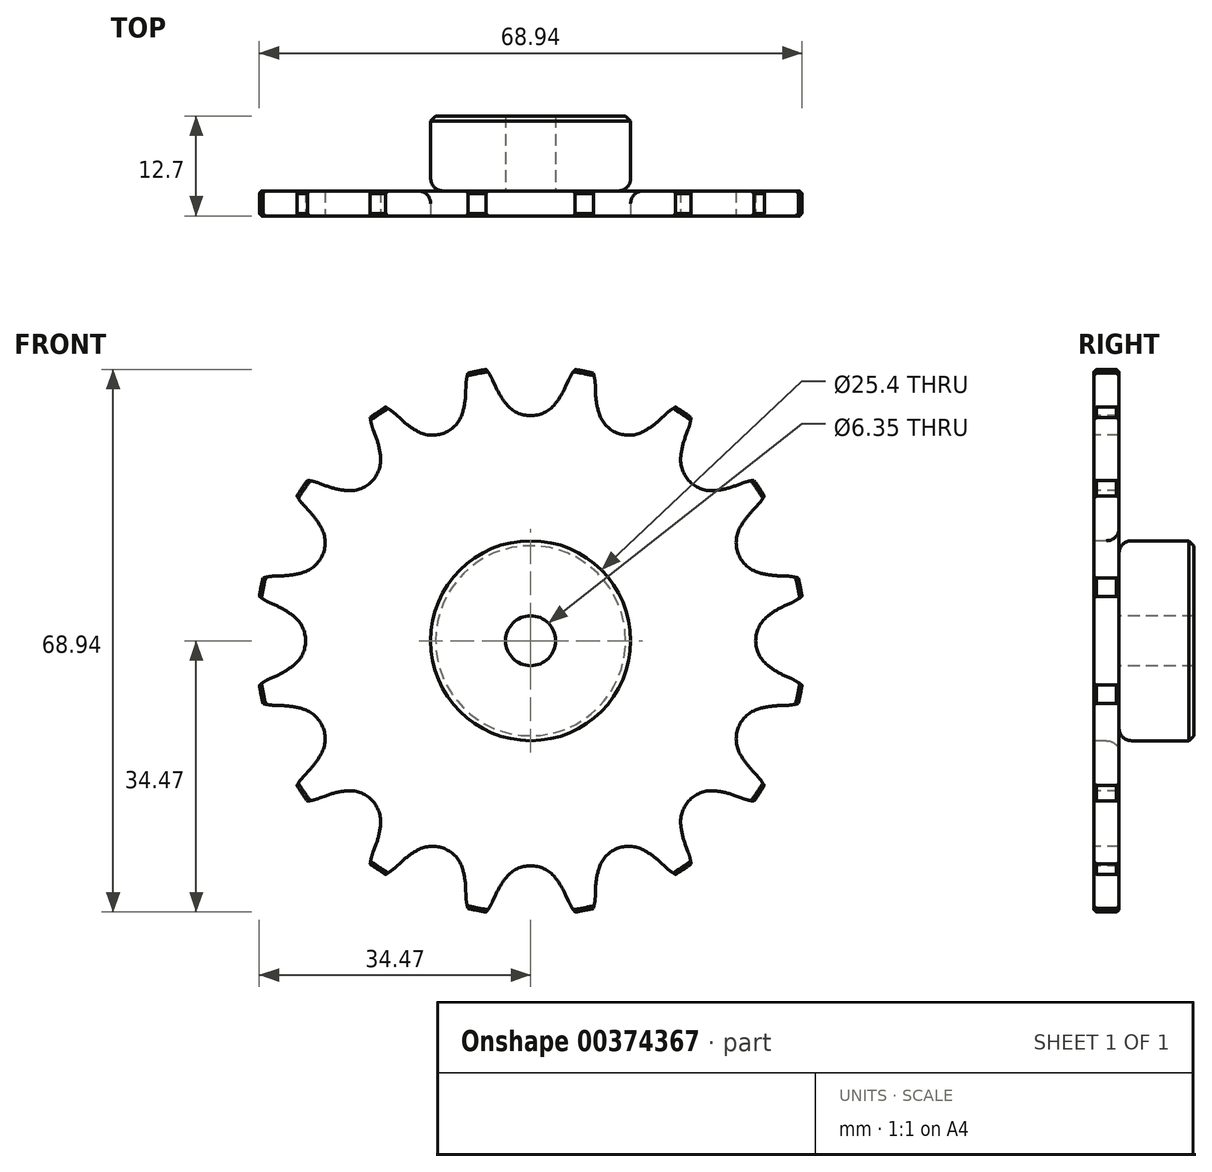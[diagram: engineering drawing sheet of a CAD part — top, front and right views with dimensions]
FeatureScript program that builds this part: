
annotation { "Feature Type Name" : "Feature", "Feature Type Description" : "" }
export const myFeature = defineFeature(function(context is Context, id is Id, definition is map)
    precondition{}
    {
        {
            assignVariable(context, id + "F0", {"name" : "Chamfer1Radius", "anyValue" : 0.64 * mm});
        }
        {
            var Q0;
            Q0=qCreatedBy(makeId("Right.planeOp"),FACE);
            var sketch = newSketch(context, id + "F1", { "sketchPlane" : qUnion([Q0])});
            skLineSegment(sketch, "E0", {"start": v(0, 0) * mm, "end": v(12.7, 0) * mm});
            skLineSegment(sketch, "E1.bottom", {"start": v(0, 3.18) * mm, "end": v(3.17, 3.18) * mm});
            skLineSegment(sketch, "E1.top", {"start": v(0, 34.93) * mm, "end": v(3.18, 34.93) * mm});
            skLineSegment(sketch, "E1.left", {"start": v(0, 3.18) * mm, "end": v(0, 34.93) * mm});
            skLineSegment(sketch, "E1.right", {"start": v(3.18, 3.18) * mm, "end": v(3.17, 34.93) * mm});
            skLineSegment(sketch, "E2.bottom", {"start": v(0, 3.18) * mm, "end": v(12.7, 3.18) * mm});
            skLineSegment(sketch, "E2.top", {"start": v(0, 12.7) * mm, "end": v(12.7, 12.7) * mm});
            skLineSegment(sketch, "E2.left", {"start": v(0, 3.18) * mm, "end": v(0, 12.7) * mm});
            skLineSegment(sketch, "E2.right", {"start": v(12.7, 3.18) * mm, "end": v(12.7, 12.7) * mm});
            skLineSegment(sketch, "E3.MirrorCS", {"start": v(0, -3.18) * mm, "end": v(3.17, -3.18) * mm});
            skLineSegment(sketch, "E4.MirrorCS", {"start": v(0, -12.7) * mm, "end": v(12.7, -12.7) * mm});
            skLineSegment(sketch, "E5.MirrorCS", {"start": v(0, -3.18) * mm, "end": v(12.7, -3.18) * mm});
            skLineSegment(sketch, "E6.MirrorCS", {"start": v(12.7, -3.18) * mm, "end": v(12.7, -12.7) * mm});
            skLineSegment(sketch, "E7.MirrorCS", {"start": v(3.18, -3.18) * mm, "end": v(3.18, -34.93) * mm});
            skLineSegment(sketch, "E8.MirrorCS", {"start": v(0, -3.18) * mm, "end": v(0, -34.93) * mm});
            skLineSegment(sketch, "E9.MirrorCS", {"start": v(0, -34.93) * mm, "end": v(3.18, -34.93) * mm});
            skLineSegment(sketch, "E10.MirrorCS", {"start": v(0, -3.18) * mm, "end": v(0, -12.7) * mm});
            skSolve(sketch);
        }
        {
            var Q0;
            {var subQ5=sQuery(id+"F1.wireOp",EDGE,"E2.right");Q0=makeQuery(id+"F1.imprint","IMPRINT",FACE,{"disambiguationData":[TD([[makeQuery(id+"F1.imprint","IMPRINT",EDGE,{"derivedFrom":subQ5}),1.0]])]});}
            var Q1;
            {var subQ5=sQuery(id+"F1.wireOp",EDGE,"E2.left");Q1=makeQuery(id+"F1.imprint","IMPRINT",FACE,{"disambiguationData":[TD([[makeQuery(id+"F1.imprint","IMPRINT",EDGE,{"derivedFrom":subQ5}),-1.0]])]});}
            var Q2;
            {var subQ0=sQuery(id+"F1.wireOp",EDGE,"E1.top");Q2=makeQuery(id+"F1.imprint","IMPRINT",FACE,{"disambiguationData":[TD([[makeQuery(id+"F1.imprint","IMPRINT",EDGE,{"derivedFrom":subQ0}),-1.0]])]});}
            var Q3;
            Q3=sQuery(id+"F1.wireOp",EDGE,"E0");
            revolve(context, id + "F2", {"entities" : qUnion([Q0, Q1, Q2]), "axis" : qUnion([Q3]), "revolveType" : RevolveType.FULL});
        }
        {
            var Q0;
            Q0=makeQuery(id+"F2.opRevolve","SWEPT_EDGE",EDGE,{"disambiguationData":[OSD([sQuery(id+"F1.wireOp",EDGE,"E1.right"),sQuery(id+"F1.wireOp",EDGE,"E2.top")])]});
            fillet(context, id + "F3", {"entities" : qUnion([Q0]), "radius" : 1.59 * mm, "tangentPropagation" : true, "allowEdgeOverflow" : false});
        }
        {
            var Q0;
            Q0=makeQuery(id+"F2.opRevolve","SWEPT_EDGE",EDGE,{"disambiguationData":[OSD([sQuery(id+"F1.wireOp",EDGE,"E2.top"),sQuery(id+"F1.wireOp",EDGE,"E2.right")])]});
            chamfer(context, id + "F4", {"entities" : qUnion([Q0]), "width" : getVariable(context, 'Chamfer1Radius'), "tangentPropagation" : true});
        }
        {
            var Q0;
            Q0=makeQuery(id+"F2.opRevolve","SWEPT_EDGE",EDGE,{"disambiguationData":[OSD([sQuery(id+"F1.wireOp",EDGE,"E1.top"),sQuery(id+"F1.wireOp",EDGE,"E1.left")])]});
            var Q1;
            Q1=makeQuery(id+"F2.opRevolve","SWEPT_EDGE",EDGE,{"disambiguationData":[OSD([sQuery(id+"F1.wireOp",EDGE,"E1.top"),sQuery(id+"F1.wireOp",EDGE,"E1.right")])]});
            chamfer(context, id + "F5", {"entities" : qUnion([Q0, Q1]), "width" : 0.32 * mm, "tangentPropagation" : true});
        }
        {
            var Q0;
            Q0=makeQuery(id+"F2.opRevolve","SWEPT_FACE",FACE,{"disambiguationData":[OSD([sQuery(id+"F1.wireOp",EDGE,"E1.left"),sQuery(id+"F1.wireOp",EDGE,"E2.left")])]});
            var sketch = newSketch(context, id + "F6", { "sketchPlane" : qUnion([Q0])});
            skCircle(sketch, "E11", {"center": v(0, 0) * mm, "radius": 32.55 * mm, "construction": true});
            skLineSegment(sketch, "E12", {"start": v(0, 0) * mm, "end": v(0, 32.55) * mm, "construction": true});
            skLineSegment(sketch, "E13", {"start": v(47.22, 32.55) * mm, "end": v(0, 32.55) * mm, "construction": true});
            skLineSegment(sketch, "E14", {"start": v(0, 32.55) * mm, "end": v(5, 36.56) * mm, "construction": true});
            skLineSegment(sketch, "E15", {"start": v(5, 36.56) * mm, "end": v(-4.46, 32.3) * mm, "construction": true});
            skLineSegment(sketch, "E16", {"start": v(-4.46, 32.3) * mm, "end": v(-4.82, 33.1) * mm});
            skLineSegment(sketch, "E17", {"start": v(0, 0) * mm, "end": v(-7.13, 35.85) * mm, "construction": true});
            skArc(sketch, "E18", {"start": v(-7.13, 35.85) * mm, "mid": v(-15.87, 26.15) * mm, "end": v(-4.82, 33.1) * mm, "construction": true});
            skArc(sketch, "E19", {"start": v(-4.82, 33.1) * mm, "mid": v(-5.78, 34.63) * mm, "end": v(-7.13, 35.85) * mm});
            skLineSegment(sketch, "E20", {"start": v(-4.82, 33.1) * mm, "end": v(-4.82, 33.1) * mm});
            skLineSegment(sketch, "E21", {"start": v(-4.46, 32.3) * mm, "end": v(-4.46, 32.3) * mm});
            skArc(sketch, "E22", {"start": v(-3.1, 30.07) * mm, "mid": v(13.83, 41.97) * mm, "end": v(-4.46, 32.3) * mm, "construction": true});
            skArc(sketch, "E23.MirrorCS", {"start": v(4.82, 33.1) * mm, "mid": v(5.78, 34.63) * mm, "end": v(7.13, 35.85) * mm});
            skArc(sketch, "E24.MirrorCS", {"start": v(4.46, 32.3) * mm, "mid": v(3.84, 31.14) * mm, "end": v(3.1, 30.07) * mm});
            skArc(sketch, "E25", {"start": v(-4.46, 32.3) * mm, "mid": v(-3.84, 31.14) * mm, "end": v(-3.1, 30.07) * mm});
            skLineSegment(sketch, "E26", {"start": v(-4.82, 33.1) * mm, "end": v(-11.63, 48.22) * mm, "construction": true});
            skLineSegment(sketch, "E27.MirrorCS", {"start": v(4.46, 32.3) * mm, "end": v(4.82, 33.1) * mm});
            skArc(sketch, "E28", {"start": v(3.1, 30.07) * mm, "mid": v(0, 36.51) * mm, "end": v(-3.1, 30.07) * mm, "construction": true});
            skArc(sketch, "E29", {"start": v(-3.1, 30.07) * mm, "mid": v(0, 28.59) * mm, "end": v(3.1, 30.07) * mm});
            skLineSegment(sketch, "E30.1.0", {"start": v(-16.48, 28.14) * mm, "end": v(-17.12, 28.74) * mm});
            skArc(sketch, "E30.1.1", {"start": v(-17.12, 28.74) * mm, "mid": v(-18.6, 29.79) * mm, "end": v(-20.3, 30.4) * mm});
            skArc(sketch, "E30.1.2", {"start": v(-14.36, 26.6) * mm, "mid": v(-10.94, 26.41) * mm, "end": v(-8.65, 28.96) * mm});
            skArc(sketch, "E30.1.3", {"start": v(-16.48, 28.14) * mm, "mid": v(-15.47, 27.3) * mm, "end": v(-14.36, 26.6) * mm});
            skArc(sketch, "E30.1.4", {"start": v(-8.24, 31.55) * mm, "mid": v(-8.37, 30.24) * mm, "end": v(-8.65, 28.96) * mm});
            skLineSegment(sketch, "E30.1.5", {"start": v(-8.24, 31.55) * mm, "end": v(-8.22, 32.42) * mm});
            skArc(sketch, "E30.1.6", {"start": v(-8.22, 32.42) * mm, "mid": v(-7.91, 34.21) * mm, "end": v(-7.13, 35.85) * mm});
            skLineSegment(sketch, "E30.2.0", {"start": v(-26, 19.69) * mm, "end": v(-26.8, 20) * mm});
            skArc(sketch, "E30.2.1", {"start": v(-26.8, 20) * mm, "mid": v(-28.58, 20.4) * mm, "end": v(-30.4, 20.3) * mm});
            skArc(sketch, "E30.2.2", {"start": v(-23.45, 19.08) * mm, "mid": v(-20.21, 20.21) * mm, "end": v(-19.08, 23.45) * mm});
            skArc(sketch, "E30.2.3", {"start": v(-26, 19.69) * mm, "mid": v(-24.74, 19.3) * mm, "end": v(-23.45, 19.08) * mm});
            skArc(sketch, "E30.2.4", {"start": v(-19.69, 26) * mm, "mid": v(-19.3, 24.74) * mm, "end": v(-19.08, 23.45) * mm});
            skLineSegment(sketch, "E30.2.5", {"start": v(-19.69, 26) * mm, "end": v(-20, 26.8) * mm});
            skArc(sketch, "E30.2.6", {"start": v(-20, 26.8) * mm, "mid": v(-20.4, 28.58) * mm, "end": v(-20.3, 30.4) * mm});
            skLineSegment(sketch, "E30.3.0", {"start": v(-31.55, 8.24) * mm, "end": v(-32.42, 8.22) * mm});
            skArc(sketch, "E30.3.1", {"start": v(-32.42, 8.22) * mm, "mid": v(-34.21, 7.91) * mm, "end": v(-35.85, 7.13) * mm});
            skArc(sketch, "E30.3.2", {"start": v(-28.96, 8.65) * mm, "mid": v(-26.41, 10.94) * mm, "end": v(-26.6, 14.36) * mm});
            skArc(sketch, "E30.3.3", {"start": v(-31.55, 8.24) * mm, "mid": v(-30.24, 8.37) * mm, "end": v(-28.96, 8.65) * mm});
            skArc(sketch, "E30.3.4", {"start": v(-28.14, 16.48) * mm, "mid": v(-27.3, 15.47) * mm, "end": v(-26.6, 14.36) * mm});
            skLineSegment(sketch, "E30.3.5", {"start": v(-28.14, 16.48) * mm, "end": v(-28.74, 17.12) * mm});
            skArc(sketch, "E30.3.6", {"start": v(-28.74, 17.12) * mm, "mid": v(-29.79, 18.6) * mm, "end": v(-30.4, 20.3) * mm});
            skLineSegment(sketch, "E30.4.0", {"start": v(-32.3, -4.46) * mm, "end": v(-33.1, -4.82) * mm});
            skArc(sketch, "E30.4.1", {"start": v(-33.1, -4.82) * mm, "mid": v(-34.63, -5.78) * mm, "end": v(-35.85, -7.13) * mm});
            skArc(sketch, "E30.4.2", {"start": v(-30.07, -3.1) * mm, "mid": v(-28.59, 0) * mm, "end": v(-30.07, 3.1) * mm});
            skArc(sketch, "E30.4.3", {"start": v(-32.3, -4.46) * mm, "mid": v(-31.14, -3.84) * mm, "end": v(-30.07, -3.1) * mm});
            skArc(sketch, "E30.4.4", {"start": v(-32.3, 4.46) * mm, "mid": v(-31.14, 3.84) * mm, "end": v(-30.07, 3.1) * mm});
            skLineSegment(sketch, "E30.4.5", {"start": v(-32.3, 4.46) * mm, "end": v(-33.1, 4.82) * mm});
            skArc(sketch, "E30.4.6", {"start": v(-33.1, 4.82) * mm, "mid": v(-34.63, 5.78) * mm, "end": v(-35.85, 7.13) * mm});
            skLineSegment(sketch, "E30.5.0", {"start": v(-28.14, -16.48) * mm, "end": v(-28.74, -17.12) * mm});
            skArc(sketch, "E30.5.1", {"start": v(-28.74, -17.12) * mm, "mid": v(-29.79, -18.6) * mm, "end": v(-30.4, -20.3) * mm});
            skArc(sketch, "E30.5.2", {"start": v(-26.6, -14.36) * mm, "mid": v(-26.41, -10.94) * mm, "end": v(-28.96, -8.65) * mm});
            skArc(sketch, "E30.5.3", {"start": v(-28.14, -16.48) * mm, "mid": v(-27.3, -15.47) * mm, "end": v(-26.6, -14.36) * mm});
            skArc(sketch, "E30.5.4", {"start": v(-31.55, -8.24) * mm, "mid": v(-30.24, -8.37) * mm, "end": v(-28.96, -8.65) * mm});
            skLineSegment(sketch, "E30.5.5", {"start": v(-31.55, -8.24) * mm, "end": v(-32.42, -8.22) * mm});
            skArc(sketch, "E30.5.6", {"start": v(-32.42, -8.22) * mm, "mid": v(-34.21, -7.91) * mm, "end": v(-35.85, -7.13) * mm});
            skLineSegment(sketch, "E30.6.0", {"start": v(-19.69, -26) * mm, "end": v(-20, -26.8) * mm});
            skArc(sketch, "E30.6.1", {"start": v(-20, -26.8) * mm, "mid": v(-20.4, -28.58) * mm, "end": v(-20.3, -30.4) * mm});
            skArc(sketch, "E30.6.2", {"start": v(-19.08, -23.45) * mm, "mid": v(-20.21, -20.21) * mm, "end": v(-23.45, -19.08) * mm});
            skArc(sketch, "E30.6.3", {"start": v(-19.69, -26) * mm, "mid": v(-19.3, -24.74) * mm, "end": v(-19.08, -23.45) * mm});
            skArc(sketch, "E30.6.4", {"start": v(-26, -19.69) * mm, "mid": v(-24.74, -19.3) * mm, "end": v(-23.45, -19.08) * mm});
            skLineSegment(sketch, "E30.6.5", {"start": v(-26, -19.69) * mm, "end": v(-26.8, -20) * mm});
            skArc(sketch, "E30.6.6", {"start": v(-26.8, -20) * mm, "mid": v(-28.58, -20.4) * mm, "end": v(-30.4, -20.3) * mm});
            skLineSegment(sketch, "E30.7.0", {"start": v(-8.24, -31.55) * mm, "end": v(-8.22, -32.42) * mm});
            skArc(sketch, "E30.7.1", {"start": v(-8.22, -32.42) * mm, "mid": v(-7.91, -34.21) * mm, "end": v(-7.13, -35.85) * mm});
            skArc(sketch, "E30.7.2", {"start": v(-8.65, -28.96) * mm, "mid": v(-10.94, -26.41) * mm, "end": v(-14.36, -26.6) * mm});
            skArc(sketch, "E30.7.3", {"start": v(-8.24, -31.55) * mm, "mid": v(-8.37, -30.24) * mm, "end": v(-8.65, -28.96) * mm});
            skArc(sketch, "E30.7.4", {"start": v(-16.48, -28.14) * mm, "mid": v(-15.47, -27.3) * mm, "end": v(-14.36, -26.6) * mm});
            skLineSegment(sketch, "E30.7.5", {"start": v(-16.48, -28.14) * mm, "end": v(-17.12, -28.74) * mm});
            skArc(sketch, "E30.7.6", {"start": v(-17.12, -28.74) * mm, "mid": v(-18.6, -29.79) * mm, "end": v(-20.3, -30.4) * mm});
            skLineSegment(sketch, "E30.8.0", {"start": v(4.46, -32.3) * mm, "end": v(4.82, -33.1) * mm});
            skArc(sketch, "E30.8.1", {"start": v(4.82, -33.1) * mm, "mid": v(5.78, -34.63) * mm, "end": v(7.13, -35.85) * mm});
            skArc(sketch, "E30.8.2", {"start": v(3.1, -30.07) * mm, "mid": v(0, -28.59) * mm, "end": v(-3.1, -30.07) * mm});
            skArc(sketch, "E30.8.3", {"start": v(4.46, -32.3) * mm, "mid": v(3.84, -31.14) * mm, "end": v(3.1, -30.07) * mm});
            skArc(sketch, "E30.8.4", {"start": v(-4.46, -32.3) * mm, "mid": v(-3.84, -31.14) * mm, "end": v(-3.1, -30.07) * mm});
            skLineSegment(sketch, "E30.8.5", {"start": v(-4.46, -32.3) * mm, "end": v(-4.82, -33.1) * mm});
            skArc(sketch, "E30.8.6", {"start": v(-4.82, -33.1) * mm, "mid": v(-5.78, -34.63) * mm, "end": v(-7.13, -35.85) * mm});
            skLineSegment(sketch, "E30.9.0", {"start": v(16.48, -28.14) * mm, "end": v(17.12, -28.74) * mm});
            skArc(sketch, "E30.9.1", {"start": v(17.12, -28.74) * mm, "mid": v(18.6, -29.79) * mm, "end": v(20.3, -30.4) * mm});
            skArc(sketch, "E30.9.2", {"start": v(14.36, -26.6) * mm, "mid": v(10.94, -26.41) * mm, "end": v(8.65, -28.96) * mm});
            skArc(sketch, "E30.9.3", {"start": v(16.48, -28.14) * mm, "mid": v(15.47, -27.3) * mm, "end": v(14.36, -26.6) * mm});
            skArc(sketch, "E30.9.4", {"start": v(8.24, -31.55) * mm, "mid": v(8.37, -30.24) * mm, "end": v(8.65, -28.96) * mm});
            skLineSegment(sketch, "E30.9.5", {"start": v(8.24, -31.55) * mm, "end": v(8.22, -32.42) * mm});
            skArc(sketch, "E30.9.6", {"start": v(8.22, -32.42) * mm, "mid": v(7.91, -34.21) * mm, "end": v(7.13, -35.85) * mm});
            skLineSegment(sketch, "E30.10.0", {"start": v(26, -19.69) * mm, "end": v(26.8, -20) * mm});
            skArc(sketch, "E30.10.1", {"start": v(26.8, -20) * mm, "mid": v(28.58, -20.4) * mm, "end": v(30.4, -20.3) * mm});
            skArc(sketch, "E30.10.2", {"start": v(23.45, -19.08) * mm, "mid": v(20.21, -20.21) * mm, "end": v(19.08, -23.45) * mm});
            skArc(sketch, "E30.10.3", {"start": v(26, -19.69) * mm, "mid": v(24.74, -19.3) * mm, "end": v(23.45, -19.08) * mm});
            skArc(sketch, "E30.10.4", {"start": v(19.69, -26) * mm, "mid": v(19.3, -24.74) * mm, "end": v(19.08, -23.45) * mm});
            skLineSegment(sketch, "E30.10.5", {"start": v(19.69, -26) * mm, "end": v(20, -26.8) * mm});
            skArc(sketch, "E30.10.6", {"start": v(20, -26.8) * mm, "mid": v(20.4, -28.58) * mm, "end": v(20.3, -30.4) * mm});
            skLineSegment(sketch, "E30.11.0", {"start": v(31.55, -8.24) * mm, "end": v(32.42, -8.22) * mm});
            skArc(sketch, "E30.11.1", {"start": v(32.42, -8.22) * mm, "mid": v(34.21, -7.91) * mm, "end": v(35.85, -7.13) * mm});
            skArc(sketch, "E30.11.2", {"start": v(28.96, -8.65) * mm, "mid": v(26.41, -10.94) * mm, "end": v(26.6, -14.36) * mm});
            skArc(sketch, "E30.11.3", {"start": v(31.55, -8.24) * mm, "mid": v(30.24, -8.37) * mm, "end": v(28.96, -8.65) * mm});
            skArc(sketch, "E30.11.4", {"start": v(28.14, -16.48) * mm, "mid": v(27.3, -15.47) * mm, "end": v(26.6, -14.36) * mm});
            skLineSegment(sketch, "E30.11.5", {"start": v(28.14, -16.48) * mm, "end": v(28.74, -17.12) * mm});
            skArc(sketch, "E30.11.6", {"start": v(28.74, -17.12) * mm, "mid": v(29.79, -18.6) * mm, "end": v(30.4, -20.3) * mm});
            skLineSegment(sketch, "E30.12.0", {"start": v(32.3, 4.46) * mm, "end": v(33.1, 4.82) * mm});
            skArc(sketch, "E30.12.1", {"start": v(33.1, 4.82) * mm, "mid": v(34.63, 5.78) * mm, "end": v(35.85, 7.13) * mm});
            skArc(sketch, "E30.12.2", {"start": v(30.07, 3.1) * mm, "mid": v(28.59, 0) * mm, "end": v(30.07, -3.1) * mm});
            skArc(sketch, "E30.12.3", {"start": v(32.3, 4.46) * mm, "mid": v(31.14, 3.84) * mm, "end": v(30.07, 3.1) * mm});
            skArc(sketch, "E30.12.4", {"start": v(32.3, -4.46) * mm, "mid": v(31.14, -3.84) * mm, "end": v(30.07, -3.1) * mm});
            skLineSegment(sketch, "E30.12.5", {"start": v(32.3, -4.46) * mm, "end": v(33.1, -4.82) * mm});
            skArc(sketch, "E30.12.6", {"start": v(33.1, -4.82) * mm, "mid": v(34.63, -5.78) * mm, "end": v(35.85, -7.13) * mm});
            skLineSegment(sketch, "E30.13.0", {"start": v(28.14, 16.48) * mm, "end": v(28.74, 17.12) * mm});
            skArc(sketch, "E30.13.1", {"start": v(28.74, 17.12) * mm, "mid": v(29.79, 18.6) * mm, "end": v(30.4, 20.3) * mm});
            skArc(sketch, "E30.13.2", {"start": v(26.6, 14.36) * mm, "mid": v(26.41, 10.94) * mm, "end": v(28.96, 8.65) * mm});
            skArc(sketch, "E30.13.3", {"start": v(28.14, 16.48) * mm, "mid": v(27.3, 15.47) * mm, "end": v(26.6, 14.36) * mm});
            skArc(sketch, "E30.13.4", {"start": v(31.55, 8.24) * mm, "mid": v(30.24, 8.37) * mm, "end": v(28.96, 8.65) * mm});
            skLineSegment(sketch, "E30.13.5", {"start": v(31.55, 8.24) * mm, "end": v(32.42, 8.22) * mm});
            skArc(sketch, "E30.13.6", {"start": v(32.42, 8.22) * mm, "mid": v(34.21, 7.91) * mm, "end": v(35.85, 7.13) * mm});
            skLineSegment(sketch, "E30.14.0", {"start": v(19.69, 26) * mm, "end": v(20, 26.8) * mm});
            skArc(sketch, "E30.14.1", {"start": v(20, 26.8) * mm, "mid": v(20.4, 28.58) * mm, "end": v(20.3, 30.4) * mm});
            skArc(sketch, "E30.14.2", {"start": v(19.08, 23.45) * mm, "mid": v(20.21, 20.21) * mm, "end": v(23.45, 19.08) * mm});
            skArc(sketch, "E30.14.3", {"start": v(19.69, 26) * mm, "mid": v(19.3, 24.74) * mm, "end": v(19.08, 23.45) * mm});
            skArc(sketch, "E30.14.4", {"start": v(26, 19.69) * mm, "mid": v(24.74, 19.3) * mm, "end": v(23.45, 19.08) * mm});
            skLineSegment(sketch, "E30.14.5", {"start": v(26, 19.69) * mm, "end": v(26.8, 20) * mm});
            skArc(sketch, "E30.14.6", {"start": v(26.8, 20) * mm, "mid": v(28.58, 20.4) * mm, "end": v(30.4, 20.3) * mm});
            skLineSegment(sketch, "E30.15.0", {"start": v(8.24, 31.55) * mm, "end": v(8.22, 32.42) * mm});
            skArc(sketch, "E30.15.1", {"start": v(8.22, 32.42) * mm, "mid": v(7.91, 34.21) * mm, "end": v(7.13, 35.85) * mm});
            skArc(sketch, "E30.15.2", {"start": v(8.65, 28.96) * mm, "mid": v(10.94, 26.41) * mm, "end": v(14.36, 26.6) * mm});
            skArc(sketch, "E30.15.3", {"start": v(8.24, 31.55) * mm, "mid": v(8.37, 30.24) * mm, "end": v(8.65, 28.96) * mm});
            skArc(sketch, "E30.15.4", {"start": v(16.48, 28.14) * mm, "mid": v(15.47, 27.3) * mm, "end": v(14.36, 26.6) * mm});
            skLineSegment(sketch, "E30.15.5", {"start": v(16.48, 28.14) * mm, "end": v(17.12, 28.74) * mm});
            skArc(sketch, "E30.15.6", {"start": v(17.12, 28.74) * mm, "mid": v(18.6, 29.79) * mm, "end": v(20.3, 30.4) * mm});
            skSolve(sketch);
        }
        {
            var Q0;
            Q0=qSketchRegion(id+"F6",true);
            extrude(context, id + "F7", {"entities" : qUnion([Q0]), "operationType" : NewBodyOperationType.INTERSECT, "endBound" : BoundingType.THROUGH_ALL, "oppositeDirection" : true, "depth" : 25.4 * mm});
        }
    });
